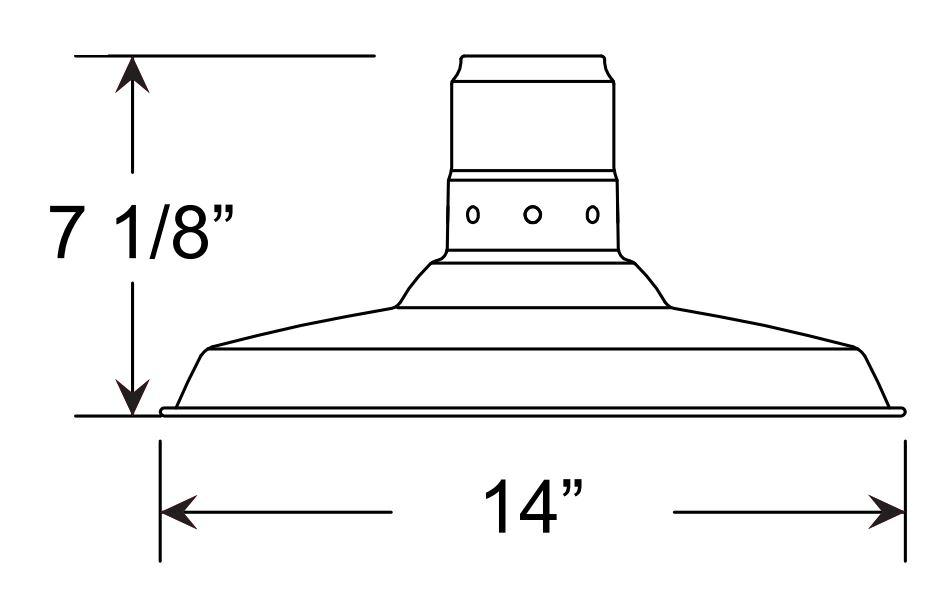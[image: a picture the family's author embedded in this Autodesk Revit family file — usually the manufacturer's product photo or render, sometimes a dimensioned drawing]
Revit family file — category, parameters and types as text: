
# Revit family: Vintage Lampshade LSU (12,14,16,18,20)MB
name_source: partatom
category: Lighting Fixtures
units: mm (PartAtom-declared; Revit-internal decimal feet)

## family parameters
Always vertical = Yes
Cut with Voids When Loaded = No
Light Source = Yes
OmniClass Number = 23.80.70.00
OmniClass Title = Lighting
Part Type = Normal
Room Calculation Point = No
Round Connector Dimension = Use Diameter
Shared = No
Work Plane-Based = No

## types (6) — shared parameters
Apparent Load = 200 VA
Body Colour = Spun aluminium
Body Material = body
Color Filter = 16777215
Construction Material = Heavy Duty spun aluminum.
Default Elevation = 0' - 0"
Description = 120-277 Voltage
Dimming Lamp Color Temperature Shift = <None>
Fixture Finish = Fixture finish
Lamp = Incandescent
Load Classification = Lighting
Manufacturer = ANP Lighting
Photometric Web File = generic.ies
Power Factor = 1
Ring = Ring
Tilt Angle = 90.00°
URL = https://www.anplighting.com
Voltage = 277 V
Warranty = 5 year limited warranty
Wattage Comments = 200W Max

## per-type parameters (varying)
| type | Fixture Diameter | Fixture Height | LSU12 | LSU14 | LSU16 | LSU18 | LSU20 | LSU22 | Weight |
| LSU12 | 1' - 0" | 1' - 3 1/2" | Yes | No | No | No | No | No | 4.2 lbs |
| LSU14 | 1' - 2" | 1' - 4" | No | Yes | No | No | No | No | 4.7lbs |
| LSU16 | 1' - 4" | 1' - 4 1/2" | No | No | Yes | No | No | No | 5.2lbs |
| LSU18 | 1' - 6" | 1' - 5" | No | No | No | Yes | No | No | 5.2lbs |
| LSU20 | 1' - 8" | 1' - 5 1/2" | No | No | No | No | Yes | No | 6.2lbs |
| LSU22 | 1' - 10" | 1' - 6" | No | No | No | No | No | Yes | 7.2lbs |

note: column(s) folded — value = type name in every type: Model

## geometry (parser evidence)
native form markers: Sweep x48
no freeform markers — native parametric forms only
